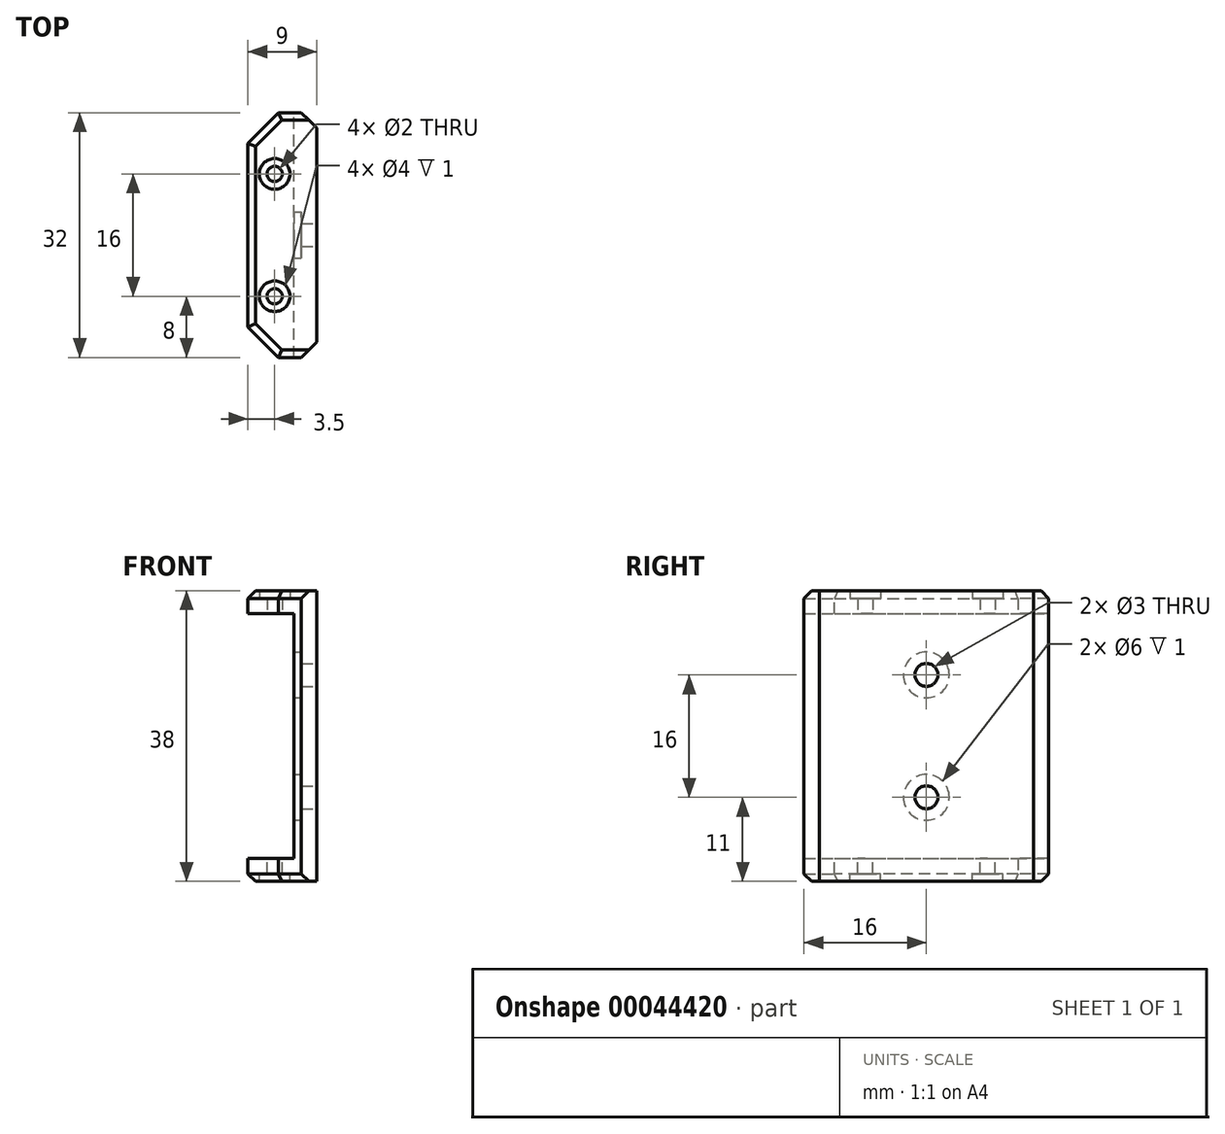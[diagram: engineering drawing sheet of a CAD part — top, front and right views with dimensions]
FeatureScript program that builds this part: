
annotation { "Feature Type Name" : "Feature", "Feature Type Description" : "" }
export const myFeature = defineFeature(function(context is Context, id is Id, definition is map)
    precondition{}
    {
        {
            var Q0;
            Q0=qCreatedBy(makeId("Front.planeOp"),FACE);
            var sketch = newSketch(context, id + "F0", { "sketchPlane" : qUnion([Q0])});
            skLineSegment(sketch, "E0.bottom", {"start": v(0, 19) * mm, "end": v(-3, 19) * mm});
            skLineSegment(sketch, "E0.top", {"start": v(0, -19) * mm, "end": v(-3, -19) * mm});
            skLineSegment(sketch, "E0.left", {"start": v(0, 19) * mm, "end": v(0, -19) * mm});
            skLineSegment(sketch, "E0.right", {"start": v(-3, 19) * mm, "end": v(-3, -19) * mm});
            skLineSegment(sketch, "E1.bottom", {"start": v(-3, 19) * mm, "end": v(-9, 19) * mm});
            skLineSegment(sketch, "E1.top", {"start": v(-3, 16) * mm, "end": v(-9, 16) * mm});
            skLineSegment(sketch, "E1.left", {"start": v(-3, 19) * mm, "end": v(-3, 16) * mm});
            skLineSegment(sketch, "E1.right", {"start": v(-9, 19) * mm, "end": v(-9, 16) * mm});
            skLineSegment(sketch, "E2.MirrorCS", {"start": v(-3, -16) * mm, "end": v(-9, -16) * mm});
            skLineSegment(sketch, "E3.MirrorCS", {"start": v(-9, -19) * mm, "end": v(-9, -16) * mm});
            skLineSegment(sketch, "E4.MirrorCS", {"start": v(-3, -19) * mm, "end": v(-9, -19) * mm});
            skSolve(sketch);
        }
        {
            var Q0;
            Q0=makeQuery(id+"F0.imprint","IMPRINT",FACE,{"disambiguationData":[TD([[makeQuery(id+"F0.imprint","IMPRINT",EDGE,{"derivedFrom":sQuery(id+"F0.wireOp",EDGE,"E1.bottom")}),1.0]])]});
            var Q1;
            Q1=makeQuery(id+"F0.imprint","IMPRINT",FACE,{"disambiguationData":[TD([[makeQuery(id+"F0.imprint","IMPRINT",EDGE,{"derivedFrom":sQuery(id+"F0.wireOp",EDGE,"E0.bottom")}),1.0]])]});
            var Q2;
            {var subQ1=sQuery(id+"F0.wireOp",EDGE,"E2.MirrorCS");Q2=makeQuery(id+"F0.imprint","IMPRINT",FACE,{"disambiguationData":[TD([[makeQuery(id+"F0.imprint","IMPRINT",EDGE,{"derivedFrom":subQ1}),1.0]])]});}
            extrude(context, id + "F1", {"entities" : qUnion([Q0, Q1, Q2]), "depth" : 32 * mm, "symmetric" : true});
        }
        {
            var Q0;
            Q0=makeQuery(id+"F1.opExtrude","SWEPT_FACE",FACE,{"disambiguationData":[OSD([sQuery(id+"F0.wireOp",EDGE,"E0.bottom"),sQuery(id+"F0.wireOp",EDGE,"E1.bottom")])]});
            var sketch = newSketch(context, id + "F2", { "sketchPlane" : qUnion([Q0])});
            skPoint(sketch, "E5", {"position": v(-5.5, 8) * mm});
            skPoint(sketch, "E6.MirrorP", {"position": v(-5.5, -8) * mm});
            skSolve(sketch);
        }
        {
            var Q0;
            Q0=sQuery(id+"F2.wireOp",VERTEX,"E5");
            var Q1;
            Q1=sQuery(id+"F2.wireOp",VERTEX,"E6.MirrorP");
            var Q2;
            Q2=makeQuery(id+"F1.opExtrude","SWEPT_BODY",BODY,{"disambiguationData":[OSD([sQuery(id+"F0.wireOp",EDGE,"E0.bottom"),sQuery(id+"F0.wireOp",EDGE,"E0.top"),sQuery(id+"F0.wireOp",EDGE,"E0.left"),sQuery(id+"F0.wireOp",EDGE,"E0.right"),sQuery(id+"F0.wireOp",EDGE,"E1.bottom"),sQuery(id+"F0.wireOp",EDGE,"E1.top"),sQuery(id+"F0.wireOp",EDGE,"E1.right"),sQuery(id+"F0.wireOp",EDGE,"E2.MirrorCS"),sQuery(id+"F0.wireOp",EDGE,"E3.MirrorCS"),sQuery(id+"F0.wireOp",EDGE,"E4.MirrorCS")])]});
            hole(context, id + "F3", {"style" : HoleStyle.C_BORE, "holeDiameter" : 2 * mm, "cBoreDiameter" : 4 * mm, "cBoreDepth" : 1 * mm, "endStyle" : HoleEndStyle.BLIND, "holeDepth" : 5 * mm, "locations" : qUnion([Q0, Q1]), "scope" : qUnion([Q2])});
        }
        {
            var Q0;
            Q0=makeQuery(id+"F1.opExtrude","SWEPT_FACE",FACE,{"disambiguationData":[OSD([sQuery(id+"F0.wireOp",EDGE,"E0.top"),sQuery(id+"F0.wireOp",EDGE,"E4.MirrorCS")])]});
            var sketch = newSketch(context, id + "F4", { "sketchPlane" : qUnion([Q0])});
            skPoint(sketch, "E7.0", {"position": v(-5.5, -8) * mm});
            skPoint(sketch, "E7.1", {"position": v(-5.5, 8) * mm});
            skSolve(sketch);
        }
        {
            var Q0;
            Q0=sQuery(id+"F4.wireOp",VERTEX,"E7.0");
            var Q1;
            Q1=sQuery(id+"F4.wireOp",VERTEX,"E7.1");
            var Q2;
            Q2=makeQuery(id+"F1.opExtrude","SWEPT_BODY",BODY,{"disambiguationData":[OSD([sQuery(id+"F0.wireOp",EDGE,"E0.bottom"),sQuery(id+"F0.wireOp",EDGE,"E0.top"),sQuery(id+"F0.wireOp",EDGE,"E0.left"),sQuery(id+"F0.wireOp",EDGE,"E0.right"),sQuery(id+"F0.wireOp",EDGE,"E1.bottom"),sQuery(id+"F0.wireOp",EDGE,"E1.top"),sQuery(id+"F0.wireOp",EDGE,"E1.right"),sQuery(id+"F0.wireOp",EDGE,"E2.MirrorCS"),sQuery(id+"F0.wireOp",EDGE,"E3.MirrorCS"),sQuery(id+"F0.wireOp",EDGE,"E4.MirrorCS")])]});
            hole(context, id + "F5", {"style" : HoleStyle.C_BORE, "holeDiameter" : 2 * mm, "cBoreDiameter" : 4 * mm, "cBoreDepth" : 1 * mm, "endStyle" : HoleEndStyle.BLIND, "holeDepth" : 5 * mm, "locations" : qUnion([Q0, Q1]), "scope" : qUnion([Q2])});
        }
        {
            var Q0;
            Q0=makeQuery(id+"F1.opExtrude","CAP_EDGE",EDGE,{"disambiguationData":[OSD([sQuery(id+"F0.wireOp",EDGE,"E1.right")])],"isStart":false});
            var Q1;
            Q1=makeQuery(id+"F1.opExtrude","CAP_EDGE",EDGE,{"disambiguationData":[OSD([sQuery(id+"F0.wireOp",EDGE,"E1.right")])],"isStart":true});
            var Q2;
            Q2=makeQuery(id+"F1.opExtrude","CAP_EDGE",EDGE,{"disambiguationData":[OSD([sQuery(id+"F0.wireOp",EDGE,"E3.MirrorCS")])],"isStart":true});
            var Q3;
            Q3=makeQuery(id+"F1.opExtrude","CAP_EDGE",EDGE,{"disambiguationData":[OSD([sQuery(id+"F0.wireOp",EDGE,"E3.MirrorCS")])],"isStart":false});
            chamfer(context, id + "F6", {"entities" : qUnion([Q0, Q1, Q2, Q3]), "width" : 4 * mm, "tangentPropagation" : true});
        }
        {
            var Q0;
            Q0=makeQuery(id+"F1.opExtrude","SWEPT_FACE",FACE,{"disambiguationData":[OSD([sQuery(id+"F0.wireOp",EDGE,"E0.right")])]});
            var sketch = newSketch(context, id + "F7", { "sketchPlane" : qUnion([Q0])});
            skPoint(sketch, "E8", {"position": v(0, 8) * mm});
            skPoint(sketch, "E9.MirrorP", {"position": v(0, -8) * mm});
            skSolve(sketch);
        }
        {
            var Q0;
            Q0=sQuery(id+"F7.wireOp",VERTEX,"E8");
            var Q1;
            Q1=sQuery(id+"F7.wireOp",VERTEX,"E9.MirrorP");
            var Q2;
            Q2=makeQuery(id+"F1.opExtrude","SWEPT_BODY",BODY,{"disambiguationData":[OSD([sQuery(id+"F0.wireOp",EDGE,"E0.bottom"),sQuery(id+"F0.wireOp",EDGE,"E0.top"),sQuery(id+"F0.wireOp",EDGE,"E0.left"),sQuery(id+"F0.wireOp",EDGE,"E0.right"),sQuery(id+"F0.wireOp",EDGE,"E1.bottom"),sQuery(id+"F0.wireOp",EDGE,"E1.top"),sQuery(id+"F0.wireOp",EDGE,"E1.right"),sQuery(id+"F0.wireOp",EDGE,"E2.MirrorCS"),sQuery(id+"F0.wireOp",EDGE,"E3.MirrorCS"),sQuery(id+"F0.wireOp",EDGE,"E4.MirrorCS")])]});
            hole(context, id + "F8", {"style" : HoleStyle.C_BORE, "holeDiameter" : 3 * mm, "cBoreDiameter" : 6 * mm, "cBoreDepth" : 1 * mm, "endStyle" : HoleEndStyle.THROUGH, "locations" : qUnion([Q0, Q1]), "scope" : qUnion([Q2])});
        }
        {
            var Q0;
            Q0=makeQuery(id+"F1.opExtrude","CAP_EDGE",EDGE,{"disambiguationData":[OSD([sQuery(id+"F0.wireOp",EDGE,"E0.bottom"),sQuery(id+"F0.wireOp",EDGE,"E1.bottom")])],"isStart":true});
            var Q1;
            Q1=makeQuery(id+"F6.opChamfer","BLEND_EDGE",EDGE,{"blendedFrom":[makeQuery(id+"F1.opExtrude","CAP_EDGE",EDGE,{"disambiguationData":[OSD([sQuery(id+"F0.wireOp",EDGE,"E1.right")])],"isStart":true}),makeQuery(id+"F1.opExtrude","SWEPT_FACE",FACE,{"disambiguationData":[OSD([sQuery(id+"F0.wireOp",EDGE,"E0.bottom"),sQuery(id+"F0.wireOp",EDGE,"E1.bottom")])]})],"blendedInto":[makeQuery(id+"F1.opExtrude","SWEPT_FACE",FACE,{"disambiguationData":[OSD([sQuery(id+"F0.wireOp",EDGE,"E0.bottom"),sQuery(id+"F0.wireOp",EDGE,"E1.bottom")])]})]});
            var Q2;
            Q2=makeQuery(id+"F1.opExtrude","SWEPT_EDGE",EDGE,{"disambiguationData":[OSD([sQuery(id+"F0.wireOp",EDGE,"E1.bottom"),sQuery(id+"F0.wireOp",EDGE,"E1.right")])]});
            var Q3;
            Q3=makeQuery(id+"F6.opChamfer","BLEND_EDGE",EDGE,{"blendedFrom":[makeQuery(id+"F1.opExtrude","CAP_EDGE",EDGE,{"disambiguationData":[OSD([sQuery(id+"F0.wireOp",EDGE,"E1.right")])],"isStart":false}),makeQuery(id+"F1.opExtrude","SWEPT_FACE",FACE,{"disambiguationData":[OSD([sQuery(id+"F0.wireOp",EDGE,"E0.bottom"),sQuery(id+"F0.wireOp",EDGE,"E1.bottom")])]})],"blendedInto":[makeQuery(id+"F1.opExtrude","SWEPT_FACE",FACE,{"disambiguationData":[OSD([sQuery(id+"F0.wireOp",EDGE,"E0.bottom"),sQuery(id+"F0.wireOp",EDGE,"E1.bottom")])]})]});
            var Q4;
            Q4=makeQuery(id+"F1.opExtrude","CAP_EDGE",EDGE,{"disambiguationData":[OSD([sQuery(id+"F0.wireOp",EDGE,"E0.bottom"),sQuery(id+"F0.wireOp",EDGE,"E1.bottom")])],"isStart":false});
            var Q5;
            Q5=makeQuery(id+"F1.opExtrude","CAP_EDGE",EDGE,{"disambiguationData":[OSD([sQuery(id+"F0.wireOp",EDGE,"E0.top"),sQuery(id+"F0.wireOp",EDGE,"E4.MirrorCS")])],"isStart":true});
            var Q6;
            Q6=makeQuery(id+"F6.opChamfer","BLEND_EDGE",EDGE,{"blendedFrom":[makeQuery(id+"F1.opExtrude","CAP_EDGE",EDGE,{"disambiguationData":[OSD([sQuery(id+"F0.wireOp",EDGE,"E3.MirrorCS")])],"isStart":true}),makeQuery(id+"F1.opExtrude","SWEPT_FACE",FACE,{"disambiguationData":[OSD([sQuery(id+"F0.wireOp",EDGE,"E0.top"),sQuery(id+"F0.wireOp",EDGE,"E4.MirrorCS")])]})],"blendedInto":[makeQuery(id+"F1.opExtrude","SWEPT_FACE",FACE,{"disambiguationData":[OSD([sQuery(id+"F0.wireOp",EDGE,"E0.top"),sQuery(id+"F0.wireOp",EDGE,"E4.MirrorCS")])]})]});
            var Q7;
            Q7=makeQuery(id+"F1.opExtrude","SWEPT_EDGE",EDGE,{"disambiguationData":[OSD([sQuery(id+"F0.wireOp",EDGE,"E3.MirrorCS"),sQuery(id+"F0.wireOp",EDGE,"E4.MirrorCS")])]});
            var Q8;
            Q8=makeQuery(id+"F6.opChamfer","BLEND_EDGE",EDGE,{"blendedFrom":[makeQuery(id+"F1.opExtrude","CAP_EDGE",EDGE,{"disambiguationData":[OSD([sQuery(id+"F0.wireOp",EDGE,"E3.MirrorCS")])],"isStart":false}),makeQuery(id+"F1.opExtrude","SWEPT_FACE",FACE,{"disambiguationData":[OSD([sQuery(id+"F0.wireOp",EDGE,"E0.top"),sQuery(id+"F0.wireOp",EDGE,"E4.MirrorCS")])]})],"blendedInto":[makeQuery(id+"F1.opExtrude","SWEPT_FACE",FACE,{"disambiguationData":[OSD([sQuery(id+"F0.wireOp",EDGE,"E0.top"),sQuery(id+"F0.wireOp",EDGE,"E4.MirrorCS")])]})]});
            var Q9;
            Q9=makeQuery(id+"F1.opExtrude","CAP_EDGE",EDGE,{"disambiguationData":[OSD([sQuery(id+"F0.wireOp",EDGE,"E0.top"),sQuery(id+"F0.wireOp",EDGE,"E4.MirrorCS")])],"isStart":false});
            chamfer(context, id + "F9", {"entities" : qUnion([Q0, Q1, Q2, Q3, Q4, Q5, Q6, Q7, Q8, Q9]), "width" : 1 * mm, "tangentPropagation" : true});
        }
        {
            var Q0;
            Q0=makeQuery(id+"F1.opExtrude","CAP_EDGE",EDGE,{"disambiguationData":[OSD([sQuery(id+"F0.wireOp",EDGE,"E0.left")])],"isStart":true});
            var Q1;
            Q1=makeQuery(id+"F1.opExtrude","CAP_EDGE",EDGE,{"disambiguationData":[OSD([sQuery(id+"F0.wireOp",EDGE,"E0.left")])],"isStart":false});
            chamfer(context, id + "F10", {"entities" : qUnion([Q0, Q1]), "width" : 2 * mm, "tangentPropagation" : true});
        }
    });
